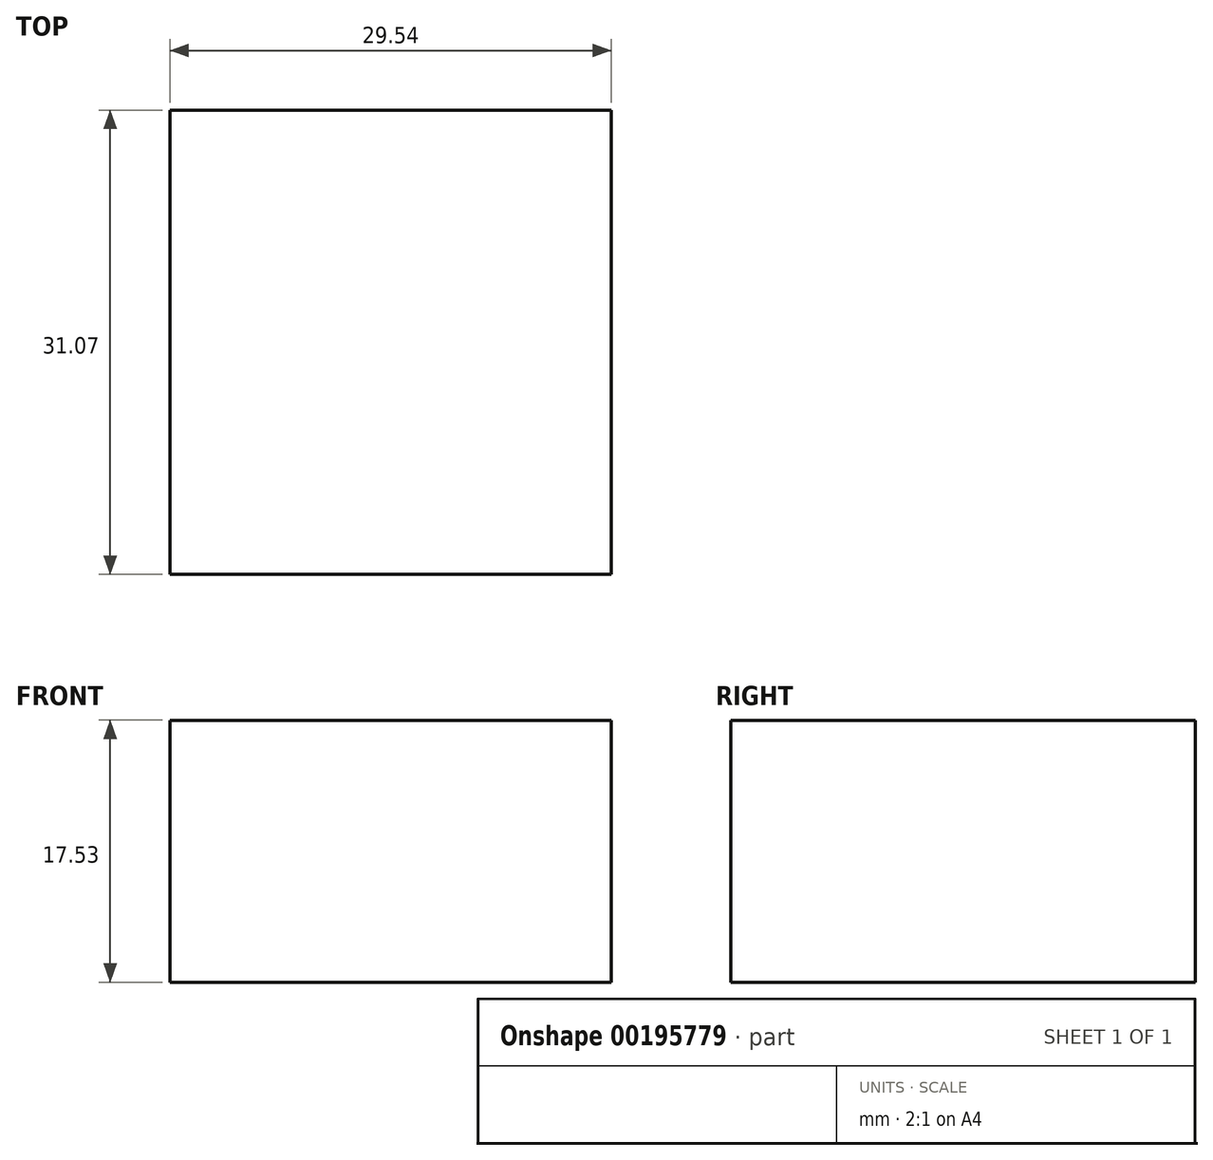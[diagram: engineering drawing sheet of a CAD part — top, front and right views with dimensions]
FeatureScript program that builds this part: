
annotation { "Feature Type Name" : "Feature", "Feature Type Description" : "" }
export const myFeature = defineFeature(function(context is Context, id is Id, definition is map)
    precondition{}
    {
        {
            var Q0;
            Q0=qCreatedBy(makeId("Top.planeOp"),FACE);
            var sketch = newSketch(context, id + "F0", { "sketchPlane" : qUnion([Q0])});
            skLineSegment(sketch, "E0.bottom", {"start": v(0, 15.07) * mm, "end": v(29.54, 15.07) * mm});
            skLineSegment(sketch, "E0.top", {"start": v(0, -16) * mm, "end": v(29.54, -16) * mm});
            skLineSegment(sketch, "E0.left", {"start": v(0, 15.07) * mm, "end": v(0, -16) * mm});
            skLineSegment(sketch, "E0.right", {"start": v(29.54, 15.07) * mm, "end": v(29.54, -16) * mm});
            skLineSegment(sketch, "E1.bottom", {"start": v(0, 31.66) * mm, "end": v(-22.69, 31.66) * mm});
            skLineSegment(sketch, "E1.top", {"start": v(0, -30.52) * mm, "end": v(-22.69, -30.52) * mm});
            skLineSegment(sketch, "E1.left", {"start": v(0, 31.66) * mm, "end": v(0, -30.52) * mm});
            skLineSegment(sketch, "E1.right", {"start": v(-22.69, 31.66) * mm, "end": v(-22.69, -30.52) * mm});
            skLineSegment(sketch, "E2.bottom", {"start": v(-22.69, 31.66) * mm, "end": v(-35.28, 31.66) * mm});
            skLineSegment(sketch, "E2.top", {"start": v(-22.69, 15.07) * mm, "end": v(-35.28, 15.07) * mm});
            skLineSegment(sketch, "E2.left", {"start": v(-22.69, 31.66) * mm, "end": v(-22.69, 15.07) * mm});
            skLineSegment(sketch, "E2.right", {"start": v(-35.28, 31.66) * mm, "end": v(-35.28, 15.07) * mm});
            skLineSegment(sketch, "E3.bottom", {"start": v(-22.69, -12.1) * mm, "end": v(-35.28, -12.1) * mm});
            skLineSegment(sketch, "E3.top", {"start": v(-22.69, -30.52) * mm, "end": v(-35.28, -30.52) * mm});
            skLineSegment(sketch, "E3.left", {"start": v(-22.69, -12.1) * mm, "end": v(-22.69, -30.52) * mm});
            skLineSegment(sketch, "E3.right", {"start": v(-35.28, -12.1) * mm, "end": v(-35.28, -30.52) * mm});
            skSolve(sketch);
        }
        {
            var Q0;
            {var subQ0=sQuery(id+"F0.wireOp",EDGE,"E0.bottom");Q0=makeQuery(id+"F0.imprint","IMPRINT",FACE,{"disambiguationData":[TD([[makeQuery(id+"F0.imprint","IMPRINT",EDGE,{"derivedFrom":subQ0}),-1.0]])]});}
            extrude(context, id + "F1", {"entities" : qUnion([Q0]), "depth" : 17.53 * mm});
        }
    });
